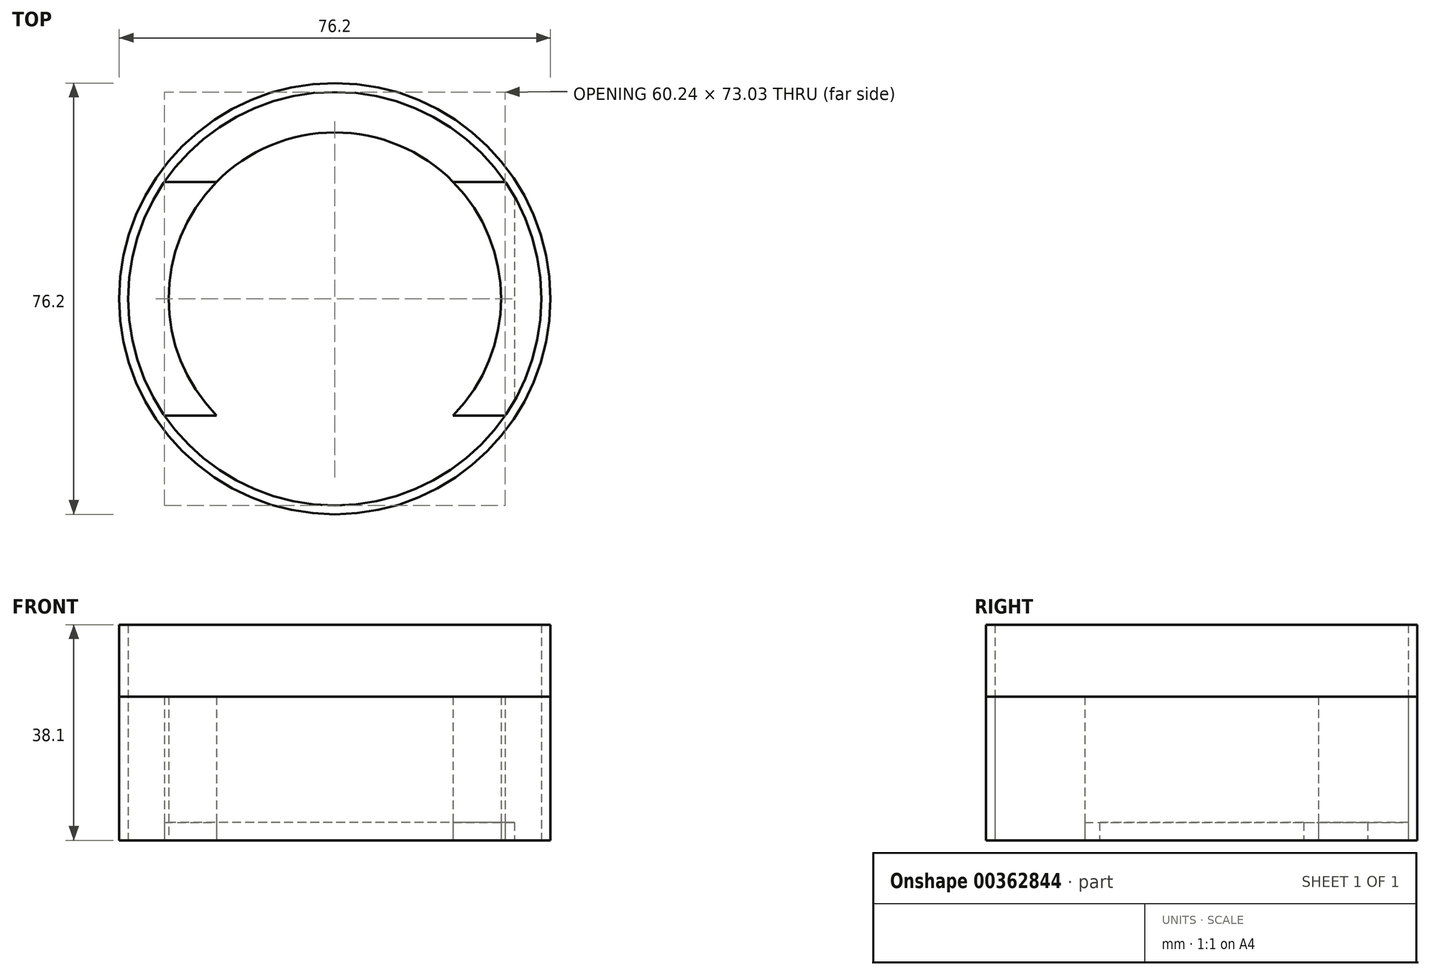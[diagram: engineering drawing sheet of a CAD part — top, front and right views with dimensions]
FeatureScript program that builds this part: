
annotation { "Feature Type Name" : "Feature", "Feature Type Description" : "" }
export const myFeature = defineFeature(function(context is Context, id is Id, definition is map)
    precondition{}
    {
        {
            var Q0;
            Q0=qCreatedBy(makeId("Top.planeOp"),FACE);
            var sketch = newSketch(context, id + "F0", { "sketchPlane" : qUnion([Q0])});
            skCircle(sketch, "E0", {"center": v(0, 0) * mm, "radius": 38.1 * mm});
            skCircle(sketch, "E1", {"center": v(0, 0) * mm, "radius": 29.37 * mm});
            skCircle(sketch, "E2", {"center": v(0, 0) * mm, "radius": 36.51 * mm});
            skLineSegment(sketch, "E3", {"start": v(-31.75, 0) * mm, "end": v(-31.75, 18.03) * mm});
            skLineSegment(sketch, "E4", {"start": v(-30.12, 20.64) * mm, "end": v(30.12, 20.64) * mm});
            skPoint(sketch, "E5.start.orphan", {"position": v(0, 46.48) * mm});
            skLineSegment(sketch, "E6.trimOffspring", {"start": v(31.75, 18.03) * mm, "end": v(31.75, -18.03) * mm});
            skLineSegment(sketch, "E7.trimOffspring", {"start": v(30.12, -20.64) * mm, "end": v(-30.12, -20.64) * mm});
            skLineSegment(sketch, "E8.trimOffspring", {"start": v(-31.75, -18.03) * mm, "end": v(-31.75, 0) * mm});
            skSolve(sketch);
        }
        {
            var Q0;
            {var subQ0=sQuery(id+"F0.wireOp",EDGE,"E4");var subQ1=sQuery(id+"F0.wireOp",EDGE,"E1");var subQ2=makeQuery(id+"F0.imprint","INTERSECT",VERTEX,{"disambiguationData":[OD(0.0)],"derivedFrom":[subQ1,subQ0]});Q0=makeQuery(id+"F0.imprint","IMPRINT",FACE,{"disambiguationData":[TD([[makeQuery(id+"F0.imprint","IMPRINT",EDGE,{"disambiguationData":[TD([[subQ2,1.0]])],"derivedFrom":subQ1}),-1.0]])]});}
            var Q1;
            {var subQ0=sQuery(id+"F0.wireOp",EDGE,"JkuErUB6-AcoL-3wLy-XnaN-httU7beqdt0P");var subQ1=sQuery(id+"F0.wireOp",EDGE,"E1");var subQ2=makeQuery(id+"F0.imprint","INTERSECT",VERTEX,{"disambiguationData":[OD(0.0)],"derivedFrom":[subQ1,subQ0]});Q1=makeQuery(id+"F0.imprint","IMPRINT",FACE,{"disambiguationData":[TD([[makeQuery(id+"F0.imprint","IMPRINT",EDGE,{"disambiguationData":[TD([[subQ2,-1.0]])],"derivedFrom":subQ1}),-1.0]])]});}
            var Q2;
            {var subQ0=sQuery(id+"F0.wireOp",EDGE,"E7.trimOffspring");var subQ1=sQuery(id+"F0.wireOp",EDGE,"E1");var subQ2=makeQuery(id+"F0.imprint","INTERSECT",VERTEX,{"disambiguationData":[OD(0.0)],"derivedFrom":[subQ1,subQ0]});Q2=makeQuery(id+"F0.imprint","IMPRINT",FACE,{"disambiguationData":[TD([[makeQuery(id+"F0.imprint","IMPRINT",EDGE,{"disambiguationData":[TD([[subQ2,-1.0]])],"derivedFrom":subQ1}),-1.0]])]});}
            extrude(context, id + "F1", {"entities" : qUnion([Q0, Q1, Q2]), "depth" : 3.17 * mm});
        }
        {
            var Q0;
            Q0=qSketchRegion(id+"F0",true);
            extrude(context, id + "F2", {"entities" : qUnion([Q0]), "depth" : 38.1 * mm});
        }
        {
            var Q0;
            {var subQ6=sQuery(id+"F0.wireOp",EDGE,"E4");var subQ7=sQuery(id+"F0.wireOp",EDGE,"E1");var subQ8=makeQuery(id+"F0.imprint","INTERSECT",VERTEX,{"disambiguationData":[OD(1.0)],"derivedFrom":[subQ7,subQ6]});Q0=makeQuery(id+"F0.imprint","IMPRINT",FACE,{"disambiguationData":[TD([[makeQuery(id+"F0.imprint","IMPRINT",EDGE,{"disambiguationData":[TD([[subQ8,1.0]])],"derivedFrom":subQ7}),-1.0]])]});}
            var Q1;
            {var subQ7=sQuery(id+"F0.wireOp",EDGE,"E4");var subQ10=sQuery(id+"F0.wireOp",EDGE,"E1");var subQ11=makeQuery(id+"F0.imprint","INTERSECT",VERTEX,{"disambiguationData":[OD(0.0)],"derivedFrom":[subQ10,subQ7]});Q1=makeQuery(id+"F0.imprint","IMPRINT",FACE,{"disambiguationData":[TD([[makeQuery(id+"F0.imprint","IMPRINT",EDGE,{"disambiguationData":[TD([[subQ11,-1.0]])],"derivedFrom":subQ10}),-1.0]])]});}
            var Q2;
            {var subQ0=sQuery(id+"F0.wireOp",EDGE,"E3");var subQ1=sQuery(id+"F0.wireOp",EDGE,"E2");var subQ2=makeQuery(id+"F0.imprint","INTERSECT",VERTEX,{"derivedFrom":[subQ1,subQ0]});Q2=makeQuery(id+"F0.imprint","IMPRINT",FACE,{"disambiguationData":[TD([[makeQuery(id+"F0.imprint","IMPRINT",EDGE,{"disambiguationData":[TD([[subQ2,-1.0]])],"derivedFrom":subQ1}),1.0]])]});}
            var Q3;
            {var subQ0=sQuery(id+"F0.wireOp",EDGE,"sCfbZfO5-3TA8-SP88-9iD4-eoFQzBwWeWFu");var subQ1=sQuery(id+"F0.wireOp",EDGE,"E2");var subQ2=makeQuery(id+"F0.imprint","INTERSECT",VERTEX,{"disambiguationData":[OD(0.0)],"derivedFrom":[subQ1,subQ0]});Q3=makeQuery(id+"F0.imprint","IMPRINT",FACE,{"disambiguationData":[TD([[makeQuery(id+"F0.imprint","IMPRINT",EDGE,{"disambiguationData":[TD([[subQ2,1.0]])],"derivedFrom":subQ1}),1.0]])]});}
            var Q4;
            {var subQ0=sQuery(id+"F0.wireOp",EDGE,"E4");var subQ1=sQuery(id+"F0.wireOp",EDGE,"E2");var subQ2=makeQuery(id+"F0.imprint","INTERSECT",VERTEX,{"disambiguationData":[OD(1.0)],"derivedFrom":[subQ1,subQ0]});Q4=makeQuery(id+"F0.imprint","IMPRINT",FACE,{"disambiguationData":[TD([[makeQuery(id+"F0.imprint","IMPRINT",EDGE,{"disambiguationData":[TD([[subQ2,-1.0]])],"derivedFrom":subQ1}),-1.0]])]});}
            var Q5;
            {var subQ0=sQuery(id+"F0.wireOp",EDGE,"0liopfZC-IP4w-TzFj-OUtP-jyX2Ku9yg7S0");var subQ1=sQuery(id+"F0.wireOp",EDGE,"E2");var subQ2=makeQuery(id+"F0.imprint","INTERSECT",VERTEX,{"derivedFrom":[subQ1,subQ0]});Q5=makeQuery(id+"F0.imprint","IMPRINT",FACE,{"disambiguationData":[TD([[makeQuery(id+"F0.imprint","IMPRINT",EDGE,{"disambiguationData":[TD([[subQ2,-1.0]])],"derivedFrom":subQ1}),-1.0]])]});}
            var Q6;
            {var subQ0=sQuery(id+"F0.wireOp",EDGE,"JkuErUB6-AcoL-3wLy-XnaN-httU7beqdt0P");var subQ1=sQuery(id+"F0.wireOp",EDGE,"E2");var subQ2=makeQuery(id+"F0.imprint","INTERSECT",VERTEX,{"disambiguationData":[OD(1.0)],"derivedFrom":[subQ1,subQ0]});Q6=makeQuery(id+"F0.imprint","IMPRINT",FACE,{"disambiguationData":[TD([[makeQuery(id+"F0.imprint","IMPRINT",EDGE,{"disambiguationData":[TD([[subQ2,-1.0]])],"derivedFrom":subQ1}),-1.0]])]});}
            var Q7;
            {var subQ0=sQuery(id+"F0.wireOp",EDGE,"E4");var subQ1=sQuery(id+"F0.wireOp",EDGE,"E2");var subQ2=makeQuery(id+"F0.imprint","INTERSECT",VERTEX,{"disambiguationData":[OD(0.0)],"derivedFrom":[subQ1,subQ0]});Q7=makeQuery(id+"F0.imprint","IMPRINT",FACE,{"disambiguationData":[TD([[makeQuery(id+"F0.imprint","IMPRINT",EDGE,{"disambiguationData":[TD([[subQ2,1.0]])],"derivedFrom":subQ1}),-1.0]])]});}
            var Q8;
            {var subQ0=sQuery(id+"F0.wireOp",EDGE,"E6.trimOffspring");Q8=makeQuery(id+"F0.imprint","IMPRINT",FACE,{"disambiguationData":[TD([[makeQuery(id+"F0.imprint","IMPRINT",EDGE,{"derivedFrom":subQ0}),1.0]])]});}
            extrude(context, id + "F3", {"entities" : qUnion([Q0, Q1, Q2, Q3, Q4, Q5, Q6, Q7, Q8]), "depth" : 25.4 * mm});
        }
    });
